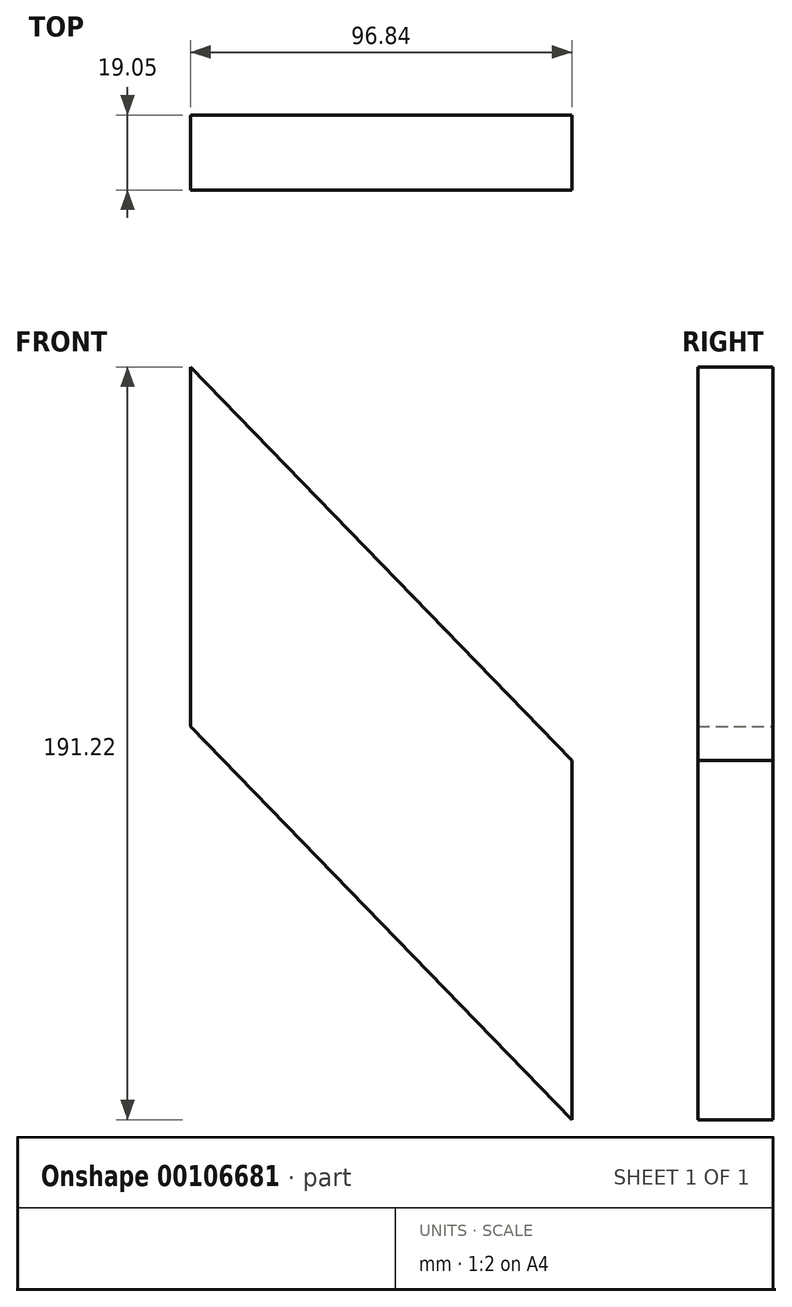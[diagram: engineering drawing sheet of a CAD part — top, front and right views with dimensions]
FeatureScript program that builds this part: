
annotation { "Feature Type Name" : "Feature", "Feature Type Description" : "" }
export const myFeature = defineFeature(function(context is Context, id is Id, definition is map)
    precondition{}
    {
        {
            var Q0;
            Q0=qCreatedBy(makeId("Front.planeOp"),FACE);
            var sketch = newSketch(context, id + "F0", { "sketchPlane" : qUnion([Q0])});
            skLineSegment(sketch, "E0", {"start": v(-189.46, 269.74) * mm, "end": v(-189.46, 178.48) * mm});
            skLineSegment(sketch, "E1", {"start": v(-189.46, 178.48) * mm, "end": v(-92.62, 78.52) * mm});
            skLineSegment(sketch, "E2", {"start": v(-92.62, 78.52) * mm, "end": v(-92.62, 169.78) * mm});
            skLineSegment(sketch, "E3", {"start": v(-92.62, 169.78) * mm, "end": v(-189.46, 269.74) * mm});
            skSolve(sketch);
        }
        {
            var Q0;
            Q0=makeQuery(id+"F0.imprint","IMPRINT",FACE,{"disambiguationData":[TD([[makeQuery(id+"F0.imprint","IMPRINT",EDGE,{"derivedFrom":sQuery(id+"F0.wireOp",EDGE,"E0")}),1.0]])]});
            extrude(context, id + "F1", {"entities" : qUnion([Q0]), "depth" : 19.05 * mm});
        }
    });
